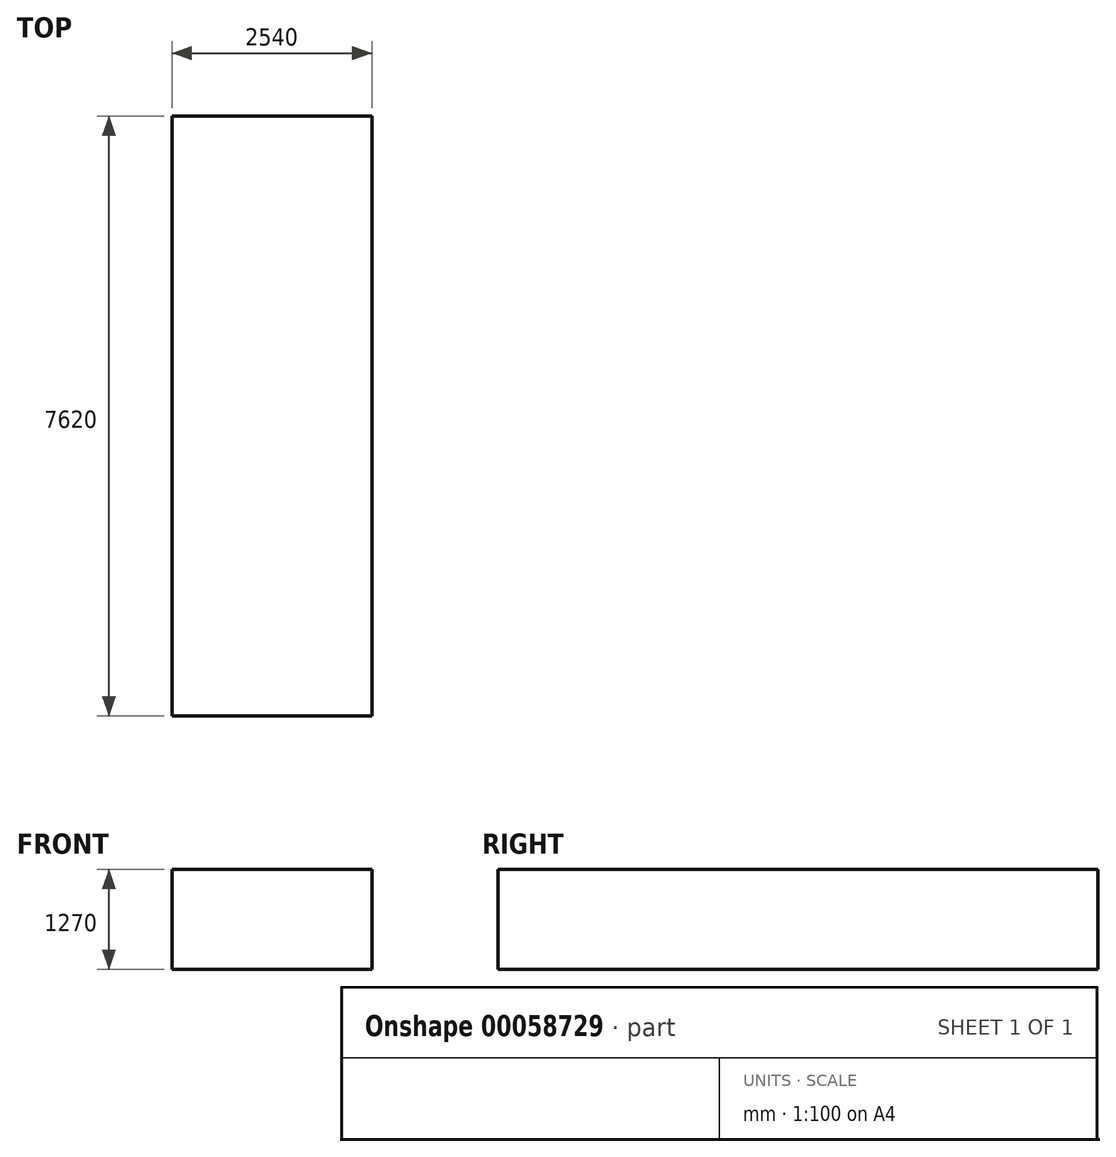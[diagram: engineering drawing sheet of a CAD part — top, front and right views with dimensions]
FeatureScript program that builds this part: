
annotation { "Feature Type Name" : "Feature", "Feature Type Description" : "" }
export const myFeature = defineFeature(function(context is Context, id is Id, definition is map)
    precondition{}
    {
        {
            var Q0;
            Q0=qCreatedBy(makeId("Top.planeOp"),FACE);
            var sketch = newSketch(context, id + "F0", { "sketchPlane" : qUnion([Q0])});
            skLineSegment(sketch, "E0.rect.bottom", {"start": v(1270, -3810) * mm, "end": v(-1270, -3810) * mm});
            skLineSegment(sketch, "E0.rect.top", {"start": v(1270, 3810) * mm, "end": v(-1270, 3810) * mm});
            skLineSegment(sketch, "E0.rect.left", {"start": v(1270, -3810) * mm, "end": v(1270, 3810) * mm});
            skLineSegment(sketch, "E0.rect.right", {"start": v(-1270, -3810) * mm, "end": v(-1270, 3810) * mm});
            skPoint(sketch, "E0.rect.middle", {"position": v(0, 0) * mm});
            skSolve(sketch);
        }
        {
            var Q0;
            Q0=makeQuery(id+"F0.imprint","IMPRINT",FACE,{"disambiguationData":[TD([[makeQuery(id+"F0.imprint","IMPRINT",EDGE,{"derivedFrom":sQuery(id+"F0.wireOp",EDGE,"E0.rect.bottom")}),-1.0]])]});
            extrude(context, id + "F1", {"entities" : qUnion([Q0]), "depth" : 1270 * mm});
        }
    });
